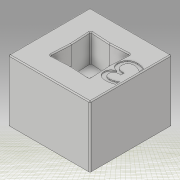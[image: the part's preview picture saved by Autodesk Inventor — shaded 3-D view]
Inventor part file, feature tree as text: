
AUTODESK INVENTOR PART (.ipt)
format: ipt  version: 2018 (Build 220112000, 112)  size: 244,224 bytes
history: native  units: in
note: dims shown in document units (in); Inventor stores cm internally (conversion verified against a paired STEP export)
features: extrude x5, sketch x5, plane x2, mirror x2, fillet x2, projected_geometry x2
ambient origin geometry x8: Origin, YZ Plane, XZ Plane, XY Plane, X Axis, Y Axis, Z Axis, Center Point
bodies: Solid1 (feature_tree)
feature tree (18):
  extrude  "Extrusion1"  Depth=2.0in
  extrude  "Extrusion2"  Depth=0.525in
  extrude  "Extrusion3"  Depth=0.941in
  plane  "Work Plane1"
  plane  "Work Plane2"
  mirror  "Mirror1"
  mirror  "Mirror2"
  fillet  "Fillet1"  Radius=0.681in
  fillet  "Fillet2"  Radius=0.05in
  extrude  "Extrusion4"  Depth=0.05in
  extrude  "Extrusion5"  Depth=0.941in TaperAngle=0.0deg
  sketch  "Sketch1"  dims[d0=2.0in d1=2.0in]
  sketch  "Sketch2"  dims[d2=1.5in d3=0.0in d5=0.525in]
  projected_geometry  "Projected Loop1"
  sketch  "Sketch3"  dims[d6=0.911in d7=0.941in d8=0.681in d9=0.0in d10=0.05in]
  sketch  "Sketch4"  dims[d11=0.05in d12=0.05in]
  sketch  "Sketch5"  dims[d13=0.05in d14=0.941in d15=0.0in d16=0.025in d17=0.025in d18=0.025in d19=0.0in d20=0.515in d21=1.0in d22=0.0in]
  projected_geometry  "Projected Loop2"
